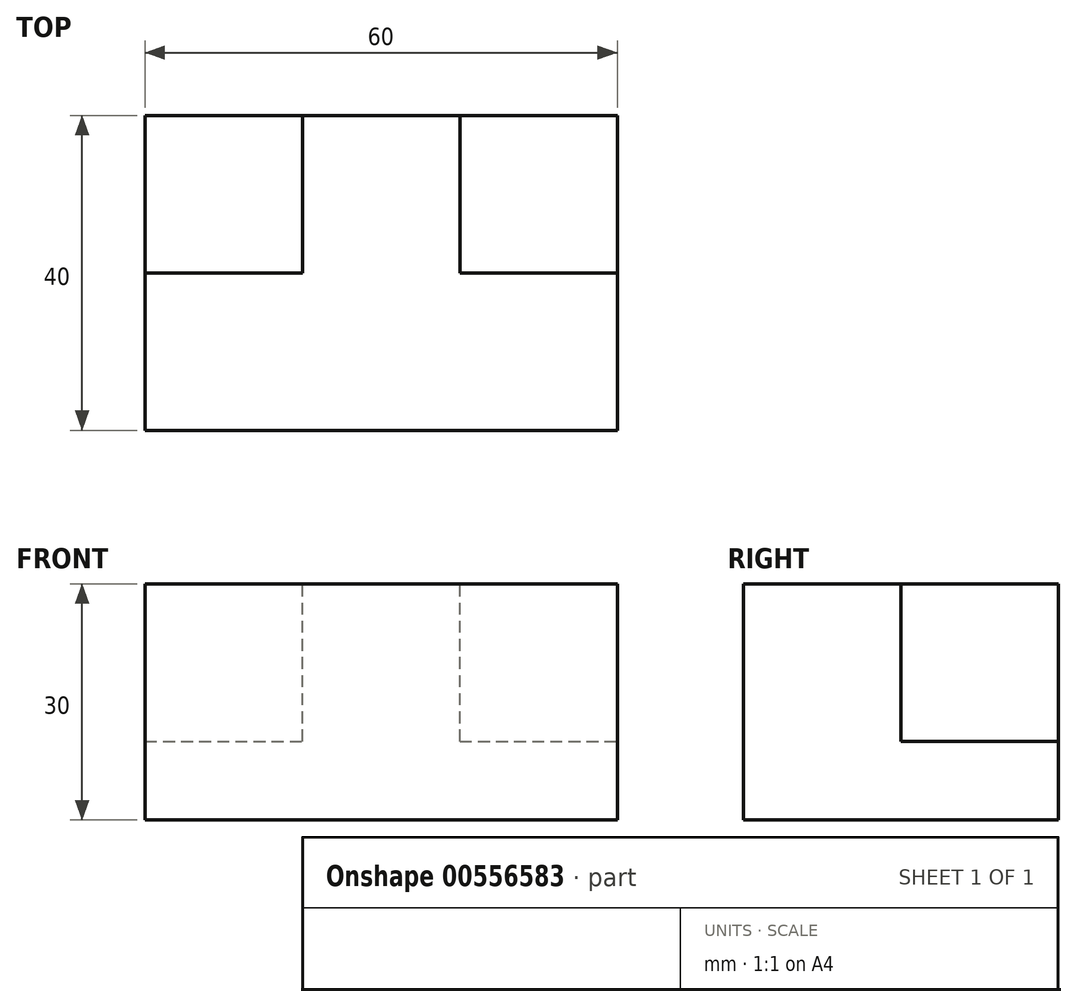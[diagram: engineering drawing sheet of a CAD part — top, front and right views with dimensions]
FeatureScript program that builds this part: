
annotation { "Feature Type Name" : "Feature", "Feature Type Description" : "" }
export const myFeature = defineFeature(function(context is Context, id is Id, definition is map)
    precondition{}
    {
        {
            var Q0;
            Q0=qCreatedBy(makeId("Top.planeOp"),FACE);
            var sketch = newSketch(context, id + "F0", { "sketchPlane" : qUnion([Q0])});
            skLineSegment(sketch, "E0.bottom", {"start": v(0, 0) * mm, "end": v(60, 0) * mm});
            skLineSegment(sketch, "E0.top", {"start": v(0, 40) * mm, "end": v(60, 40) * mm});
            skLineSegment(sketch, "E0.left", {"start": v(0, 0) * mm, "end": v(0, 40) * mm});
            skLineSegment(sketch, "E0.right", {"start": v(60, 0) * mm, "end": v(60, 40) * mm});
            skSolve(sketch);
        }
        {
            var Q0;
            Q0=makeQuery(id+"F0.imprint","IMPRINT",FACE,{"disambiguationData":[TD([[makeQuery(id+"F0.imprint","IMPRINT",EDGE,{"derivedFrom":sQuery(id+"F0.wireOp",EDGE,"E0.bottom")}),1.0]])]});
            extrude(context, id + "F1", {"entities" : qUnion([Q0]), "depth" : 30 * mm, "offsetDistance" : 25 * mm});
        }
        {
            var Q0;
            Q0=makeQuery(id+"F1.opExtrude","CAP_FACE",FACE,{"disambiguationData":[OSD([sQuery(id+"F0.wireOp",EDGE,"E0.bottom"),sQuery(id+"F0.wireOp",EDGE,"E0.top"),sQuery(id+"F0.wireOp",EDGE,"E0.left"),sQuery(id+"F0.wireOp",EDGE,"E0.right")])],"isStart":false});
            var sketch = newSketch(context, id + "F2", { "sketchPlane" : qUnion([Q0])});
            skLineSegment(sketch, "E1", {"start": v(60, 40) * mm, "end": v(60, 20) * mm});
            skLineSegment(sketch, "E2", {"start": v(60, 20) * mm, "end": v(40, 20) * mm});
            skLineSegment(sketch, "E3", {"start": v(40, 20) * mm, "end": v(40, 40) * mm});
            skLineSegment(sketch, "E4", {"start": v(0, 20) * mm, "end": v(20, 20) * mm});
            skLineSegment(sketch, "E5", {"start": v(20, 20) * mm, "end": v(20, 40) * mm});
            skSolve(sketch);
        }
        {
            var Q0;
            {var subQ0=sQuery(id+"F2.wireOp",EDGE,"E4");Q0=makeQuery(id+"F2.imprint","IMPRINT",FACE,{"disambiguationData":[TD([[makeQuery(id+"F2.imprint","IMPRINT",EDGE,{"derivedFrom":subQ0}),1.0]])]});}
            var Q1;
            {var subQ0=sQuery(id+"F2.wireOp",EDGE,"E1");Q1=makeQuery(id+"F2.imprint","IMPRINT",FACE,{"disambiguationData":[TD([[makeQuery(id+"F2.imprint","IMPRINT",EDGE,{"derivedFrom":subQ0}),1.0]])]});}
            extrude(context, id + "F3", {"entities" : qUnion([Q0, Q1]), "operationType" : NewBodyOperationType.REMOVE, "oppositeDirection" : true, "depth" : 20 * mm, "offsetDistance" : 25 * mm});
        }
    });
